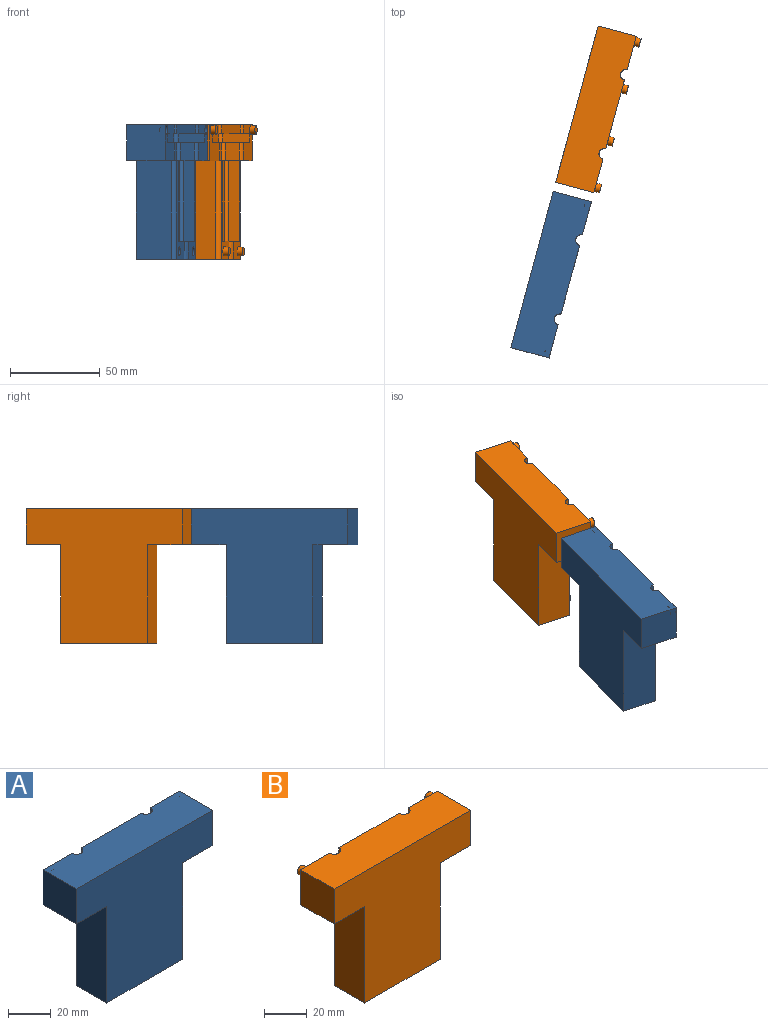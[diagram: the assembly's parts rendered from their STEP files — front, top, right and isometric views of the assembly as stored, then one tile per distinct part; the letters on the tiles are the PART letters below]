
ASSEMBLY  parts=2 mates=4
PART A: 46 faces, bbox 90x22x75 mm
  f0: plane 20x19.25mm, normal (0,1,0), area 296.5mm2, adj f6,f9,f11,f13,f16,f17,f35,f37
  f1: plane 39.64x5mm, normal (0,1,0), area 198.2mm2, adj f9,f13,f36,f37
  f2: plane 55x15.28mm, normal (0,1,0), area 232mm2, adj f25,f28,f31,f32,f33,f35,f40
  f3: plane 55x15.41mm, normal (0,1,0), area 239.2mm2, adj f25,f27,f31,f32,f33,f34,f38
  f4: plane 22x20mm, normal (0,0,-1), area 438.7mm2, adj f5,f7,f8,f23,f34
  f5: plane 90x75mm, normal (0,-1,0), area 4550mm2, adj f4,f6,f8,f9,f17,f23,f24,f31
  f6: plane 22x20mm, normal (1,0,0), area 440mm2, adj f0,f5,f9,f17
  f7: plane 20x19.11mm, normal (0,1,0), area 294.6mm2, adj f4,f8,f9,f10,f13,f16,f34,f36
  f8: plane 22x20mm, normal (-1,0,0), area 440mm2, adj f4,f5,f7,f9
  f9: plane 90x22mm, normal (0,0,1), area 1951.9mm2, adj f0,f1,f5,f6,f7,f8,f36,f37
  f10: plane 15.29x5mm, normal (1,0.02,0), area 76.4mm2, adj f7,f13,f15,f16
  f11: plane 15.29x5mm, normal (-1,0.02,0), area 76.4mm2, adj f0,f13,f14,f16
  f12: plane 74.47x5mm, normal (0,1,0), area 372.3mm2, adj f13,f14,f15,f16
  f13: plane 79x17.25mm, normal (0,0,-1), area 1327.8mm2, adj f0,f1,f7,f10,f11,f12,f14,f15
  f14: cylinder r=2mm len=5mm, axis (0,0,1), area 15.5mm2, adj f11,f12,f13,f16
  f15: cylinder r=2mm len=5mm, axis (0,0,-1), area 15.5mm2, adj f10,f12,f13,f16
  f16: plane 79x17.25mm, normal (0,0,1), area 909.8mm2, adj f0,f7,f10,f11,f12,f14,f15,f18
  f17: plane 22x20mm, normal (0,0,-1), area 439mm2, adj f0,f5,f6,f24,f35
  f18: plane 36x10mm, normal (0,1,0), area 360mm2, adj f16,f21,f22,f25
  f19: plane 10x7.69mm, normal (1,0,0), area 76.9mm2, adj f16,f22,f25,f34
  f20: plane 10x7.32mm, normal (-1,0,0), area 73.2mm2, adj f16,f21,f25,f35
  f21: cylinder r=2mm len=10mm, axis (0,0,1), area 31.4mm2, adj f16,f18,f20,f25
  f22: cylinder r=2mm len=10mm, axis (0,0,1), area 31.4mm2, adj f16,f18,f19,f25
  f23: plane 55x19.88mm, normal (-1,0,0), area 1093.6mm2, adj f4,f5,f31,f34
  f24: plane 55x20.02mm, normal (1,0,0), area 1101.3mm2, adj f5,f17,f31,f35
  f25: plane 40x10.5mm, normal (0,0,1), area 140.8mm2, adj f2,f3,f18,f19,f20,f21,f22,f26
  f26: plane 45x30.79mm, normal (0,1,0), area 1385.5mm2, adj f25,f29,f30,f32
  f27: plane 45x6.04mm, normal (1,0.02,0), area 271.6mm2, adj f3,f25,f29,f32
  f28: plane 45x6.04mm, normal (-1,0.02,0), area 271.6mm2, adj f2,f25,f30,f32
  f29: cylinder r=2mm len=45mm, axis (0,0,1), area 139.8mm2, adj f25,f26,f27,f32
  f30: cylinder r=2mm len=45mm, axis (0,0,1), area 139.8mm2, adj f25,f26,f28,f32
  f31: plane 50x22mm, normal (0,0,-1), area 1034.9mm2, adj f2,f3,f5,f23,f24,f33,f34,f35
  f32: plane 35x8mm, normal (0,0,1), area 245.8mm2, adj f2,f3,f26,f27,f28,f29,f30,f33
  f33: cone r=5mm half-angle=3deg, axis (0,0,-1), area 149.1mm2, adj f2,f3,f31,f32
  f34: cylinder r=3mm len=65mm, axis (0,0,1), area 473.4mm2, adj f3,f4,f7,f16,f19,f23,f25,f31
  f35: cylinder r=3mm len=65mm, axis (0,0,1), area 480mm2, adj f0,f2,f16,f17,f20,f24,f25,f31
  f36: cylinder r=3mm len=6mm, axis (0,0,1), area 47mm2, adj f1,f7,f9,f13
  f37: cylinder r=3mm len=6mm, axis (0,0,1), area 47mm2, adj f0,f1,f9,f13
  f38: cone r=2.5mm half-angle=3deg, axis (0,-1,0), area 50.3mm2, adj f3,f39
  f39: plane 5.33x5.33mm, normal (0,1,0), area 22.3mm2, adj f38
  f40: cone r=2.5mm half-angle=3deg, axis (0,-1,0), area 50.3mm2, adj f2,f41
  f41: plane 5.33x5.33mm, normal (0,1,0), area 22.3mm2, adj f40
  f42: cone r=2.5mm half-angle=3deg, axis (0,-1,0), area 50.3mm2, adj f7,f43
  f43: plane 5.33x5.33mm, normal (0,1,0), area 22.3mm2, adj f42
  f44: cone r=2.5mm half-angle=3deg, axis (0,-1,0), area 50.3mm2, adj f0,f45
  f45: plane 5.33x5.33mm, normal (0,1,0), area 22.3mm2, adj f44
PART B: 46 faces, bbox 90x25x75 mm
  f0: plane 20x19.25mm, normal (0,1,0), area 296.5mm2, adj f6,f9,f11,f13,f16,f17,f35,f37
  f1: plane 39.64x5mm, normal (0,1,0), area 198.2mm2, adj f9,f13,f36,f37
  f2: plane 55x15.28mm, normal (0,1,0), area 232mm2, adj f25,f28,f31,f32,f33,f35,f38
  f3: plane 55x15.41mm, normal (0,1,0), area 239.2mm2, adj f25,f27,f31,f32,f33,f34,f40
  f4: plane 22x20mm, normal (0,0,-1), area 438.7mm2, adj f5,f7,f8,f23,f34
  f5: plane 90x75mm, normal (0,-1,0), area 4550mm2, adj f4,f6,f8,f9,f17,f23,f24,f31
  f6: plane 22x20mm, normal (1,0,0), area 440mm2, adj f0,f5,f9,f17
  f7: plane 20x19.11mm, normal (0,1,0), area 294.6mm2, adj f4,f8,f9,f10,f13,f16,f34,f36
  f8: plane 22x20mm, normal (-1,0,0), area 440mm2, adj f4,f5,f7,f9
  f9: plane 90x22mm, normal (0,0,1), area 1951.9mm2, adj f0,f1,f5,f6,f7,f8,f36,f37
  f10: plane 15.29x5mm, normal (1,0.02,0), area 76.4mm2, adj f7,f13,f15,f16
  f11: plane 15.29x5mm, normal (-1,0.02,0), area 76.4mm2, adj f0,f13,f14,f16
  f12: plane 74.47x5mm, normal (0,1,0), area 372.3mm2, adj f13,f14,f15,f16
  f13: plane 79x17.25mm, normal (0,0,-1), area 1327.8mm2, adj f0,f1,f7,f10,f11,f12,f14,f15
  f14: cylinder r=2mm len=5mm, axis (0,0,1), area 15.5mm2, adj f11,f12,f13,f16
  f15: cylinder r=2mm len=5mm, axis (0,0,-1), area 15.5mm2, adj f10,f12,f13,f16
  f16: plane 79x17.25mm, normal (0,0,1), area 909.8mm2, adj f0,f7,f10,f11,f12,f14,f15,f18
  f17: plane 22x20mm, normal (0,0,-1), area 439mm2, adj f0,f5,f6,f24,f35
  f18: plane 36x10mm, normal (0,1,0), area 360mm2, adj f16,f21,f22,f25
  f19: plane 10x7.69mm, normal (1,0,0), area 76.9mm2, adj f16,f22,f25,f34
  f20: plane 10x7.32mm, normal (-1,0,0), area 73.2mm2, adj f16,f21,f25,f35
  f21: cylinder r=2mm len=10mm, axis (0,0,1), area 31.4mm2, adj f16,f18,f20,f25
  f22: cylinder r=2mm len=10mm, axis (0,0,1), area 31.4mm2, adj f16,f18,f19,f25
  f23: plane 55x19.88mm, normal (-1,0,0), area 1093.6mm2, adj f4,f5,f31,f34
  f24: plane 55x20.02mm, normal (1,0,0), area 1101.3mm2, adj f5,f17,f31,f35
  f25: plane 40x10.5mm, normal (0,0,1), area 140.8mm2, adj f2,f3,f18,f19,f20,f21,f22,f26
  f26: plane 45x30.79mm, normal (0,1,0), area 1385.5mm2, adj f25,f29,f30,f32
  f27: plane 45x6.04mm, normal (1,0.02,0), area 271.6mm2, adj f3,f25,f29,f32
  f28: plane 45x6.04mm, normal (-1,0.02,0), area 271.6mm2, adj f2,f25,f30,f32
  f29: cylinder r=2mm len=45mm, axis (0,0,1), area 139.8mm2, adj f25,f26,f27,f32
  f30: cylinder r=2mm len=45mm, axis (0,0,1), area 139.8mm2, adj f25,f26,f28,f32
  f31: plane 50x22mm, normal (0,0,-1), area 1034.9mm2, adj f2,f3,f5,f23,f24,f33,f34,f35
  f32: plane 35x8mm, normal (0,0,1), area 245.8mm2, adj f2,f3,f26,f27,f28,f29,f30,f33
  f33: cone r=5mm half-angle=3deg, axis (0,0,-1), area 149.1mm2, adj f2,f3,f31,f32
  f34: cylinder r=3mm len=65mm, axis (0,0,1), area 473.4mm2, adj f3,f4,f7,f16,f19,f23,f25,f31
  f35: cylinder r=3mm len=65mm, axis (0,0,1), area 480mm2, adj f0,f2,f16,f17,f20,f24,f25,f31
  f36: cylinder r=3mm len=6mm, axis (0,0,1), area 47mm2, adj f1,f7,f9,f13
  f37: cylinder r=3mm len=6mm, axis (0,0,1), area 47mm2, adj f0,f1,f9,f13
  f38: cone r=2.5mm half-angle=3deg, axis (0,-1,0), area 45.7mm2, adj f2,f39
  f39: plane 4.69x4.69mm, normal (0,1,0), area 17.2mm2, adj f38
  f40: cone r=2.5mm half-angle=3deg, axis (0,-1,0), area 45.7mm2, adj f3,f41
  f41: plane 4.69x4.69mm, normal (0,1,0), area 17.2mm2, adj f40
  f42: cone r=2.5mm half-angle=3deg, axis (0,-1,0), area 45.7mm2, adj f0,f43
  f43: plane 4.69x4.69mm, normal (0,1,0), area 17.2mm2, adj f42
  f44: cone r=2.5mm half-angle=3deg, axis (0,-1,0), area 45.7mm2, adj f7,f45
  f45: plane 4.69x4.69mm, normal (0,1,0), area 17.2mm2, adj f44
PLACE A rot(axis=(0,0,-1),105.2deg) t=(139.4,-122.93,80.3)mm
PLACE B rot(axis=(0,0,-1),105.2deg) t=(164.31,-30.95,80.3)mm
MATE planar B.f7 <-> A.f0  axis (0.97,-0.26,0) through (130.6,14.9,70.3)mm
MATE planar B.f31 <-> A.f31  axis (0,0,-1) through (116.17,-38.38,15.3)mm
MATE planar B.f5 <-> A.f5  axis (-0.97,0.26,0) through (100.1,-13.56,57.63)mm
MATE planar A.f7 <-> B.f0  axis (0.97,-0.26,0) through (105.74,-76.89,79.25)mm
